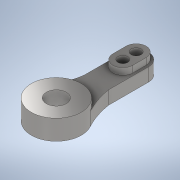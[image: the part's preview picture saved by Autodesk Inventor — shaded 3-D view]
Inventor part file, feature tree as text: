
AUTODESK INVENTOR PART (.ipt)
format: ipt  version: 2020 (Build 240168000, 168)  size: 155,136 bytes
history: native  units: in
note: dims shown in document units (in); Inventor stores cm internally (conversion verified against a paired STEP export)
features: extrude x3, sketch x3, projected_geometry x1
ambient origin geometry x8: Origin, YZ Plane, XZ Plane, XY Plane, X Axis, Y Axis, Z Axis, Center Point
bodies: Solid1 (feature_tree)
feature tree (7):
  extrude  "Extrusion1"  Depth=0.9449in
  extrude  "Extrusion2"  Depth=1.0236in
  extrude  "Extrusion3"  Depth=0.1181in
  sketch  "Sketch1"  dims[d0=0.5906in d1=0.9449in]
  sketch  "Sketch2"  dims[d2=0.2953in d3=1.0236in]
  projected_geometry  "Projected Loop1"
  sketch  "Sketch3"  dims[d4=0.1181in d5=0.1181in d6=0.7874in d7=0.2362in d8=0.0in d9=0.2362in d10=0.0787in d11=0.0in d12=0.2362in d13=0.0in d14=0.0in]
